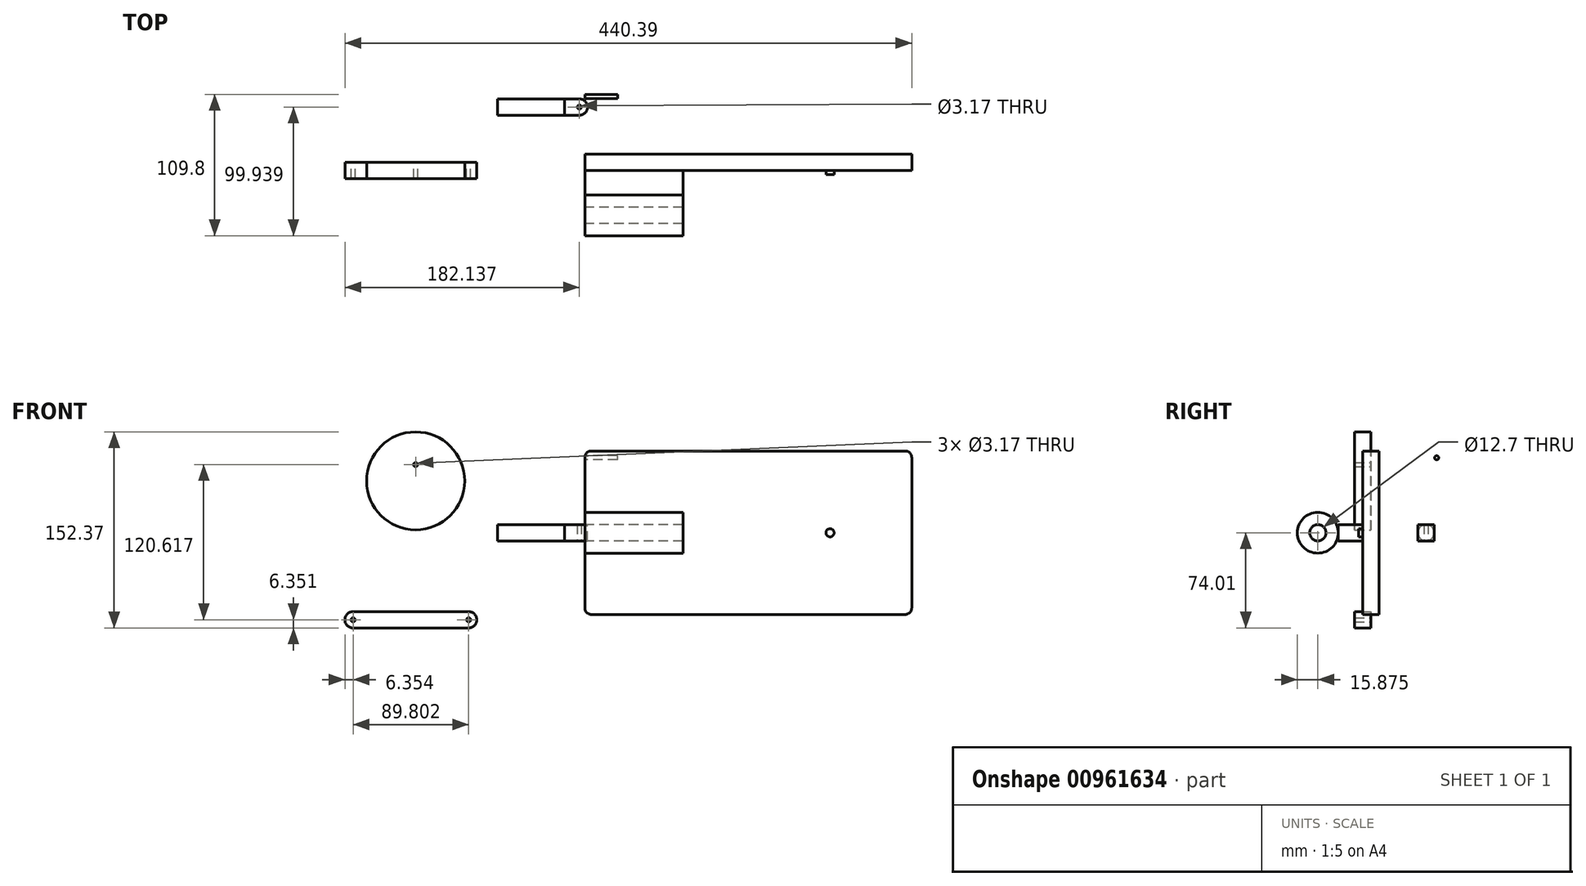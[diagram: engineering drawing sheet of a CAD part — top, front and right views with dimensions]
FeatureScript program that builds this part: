
annotation { "Feature Type Name" : "Feature", "Feature Type Description" : "" }
export const myFeature = defineFeature(function(context is Context, id is Id, definition is map)
    precondition{}
    {
        {
            var Q0;
            Q0=qCreatedBy(makeId("Right.planeOp"),FACE);
            var sketch = newSketch(context, id + "F0", { "sketchPlane" : qUnion([Q0])});
            skLineSegment(sketch, "E0.bottom", {"start": v(6.35, 63.5) * mm, "end": v(-6.35, 63.5) * mm});
            skLineSegment(sketch, "E0.top", {"start": v(6.35, -63.5) * mm, "end": v(-6.35, -63.5) * mm});
            skLineSegment(sketch, "E0.left", {"start": v(6.35, 63.5) * mm, "end": v(6.35, -63.5) * mm});
            skLineSegment(sketch, "E0.right", {"start": v(-6.35, 63.5) * mm, "end": v(-6.35, -63.5) * mm});
            skPoint(sketch, "E0.middle", {"position": v(0, 0) * mm});
            skLineSegment(sketch, "E1", {"start": v(0, 0) * mm, "end": v(-67.64, 0) * mm});
            skLineSegment(sketch, "E2.bottom", {"start": v(-6.35, 0) * mm, "end": v(-25.4, 0) * mm});
            skLineSegment(sketch, "E2.top", {"start": v(-6.35, 6.35) * mm, "end": v(-25.4, 6.35) * mm});
            skLineSegment(sketch, "E2.left", {"start": v(-6.35, 0) * mm, "end": v(-6.35, 6.35) * mm});
            skLineSegment(sketch, "E2.right", {"start": v(-25.4, 0) * mm, "end": v(-25.4, 6.35) * mm});
            skLineSegment(sketch, "E3.MirrorCS", {"start": v(-6.35, -6.35) * mm, "end": v(-25.4, -6.35) * mm});
            skLineSegment(sketch, "E4.MirrorCS", {"start": v(-25.4, 0) * mm, "end": v(-25.4, -6.35) * mm});
            skCircle(sketch, "E5", {"center": v(-41.28, 0) * mm, "radius": 15.88 * mm});
            skCircle(sketch, "E6.0", {"center": v(-41.28, 0) * mm, "radius": 6.35 * mm});
            skLineSegment(sketch, "E7", {"start": v(-6.35, 6.35) * mm, "end": v(-6.35, -6.35) * mm});
            skSolve(sketch);
        }
        {
            var Q0;
            {var subQ1=sQuery(id+"F0.wireOp",EDGE,"E0.bottom");Q0=makeQuery(id+"F0.imprint","IMPRINT",FACE,{"disambiguationData":[TD([[makeQuery(id+"F0.imprint","IMPRINT",EDGE,{"derivedFrom":subQ1}),1.0]])]});}
            extrude(context, id + "F1", {"entities" : qUnion([Q0]), "depth" : 254 * mm, "offsetDistance" : 25.4 * mm});
        }
        {
            var Q0;
            {var subQ3=sQuery(id+"F0.wireOp",EDGE,"E2.top");Q0=makeQuery(id+"F0.imprint","IMPRINT",FACE,{"disambiguationData":[TD([[makeQuery(id+"F0.imprint","IMPRINT",EDGE,{"derivedFrom":subQ3}),1.0]])]});}
            var Q1;
            {var subQ0=sQuery(id+"F0.wireOp",EDGE,"E3.MirrorCS");Q1=makeQuery(id+"F0.imprint","IMPRINT",FACE,{"disambiguationData":[TD([[makeQuery(id+"F0.imprint","IMPRINT",EDGE,{"derivedFrom":subQ0}),-1.0]])]});}
            var Q2;
            {var subQ0=sQuery(id+"F0.wireOp",EDGE,"E5");var subQ1=sQuery(id+"F0.wireOp",EDGE,"E1");var subQ5=makeQuery(id+"F0.imprint","INTERSECT",VERTEX,{"derivedFrom":[subQ1,subQ0]});Q2=makeQuery(id+"F0.imprint","IMPRINT",FACE,{"disambiguationData":[TD([[makeQuery(id+"F0.imprint","IMPRINT",EDGE,{"disambiguationData":[TD([[subQ5,1.0]])],"derivedFrom":subQ1}),1.0]])]});}
            var Q3;
            {var subQ0=sQuery(id+"F0.wireOp",EDGE,"E5");var subQ1=sQuery(id+"F0.wireOp",EDGE,"E1");var subQ5=makeQuery(id+"F0.imprint","INTERSECT",VERTEX,{"derivedFrom":[subQ1,subQ0]});Q3=makeQuery(id+"F0.imprint","IMPRINT",FACE,{"disambiguationData":[TD([[makeQuery(id+"F0.imprint","IMPRINT",EDGE,{"disambiguationData":[TD([[subQ5,1.0]])],"derivedFrom":subQ1}),-1.0]])]});}
            extrude(context, id + "F2", {"entities" : qUnion([Q0, Q1, Q2, Q3]), "operationType" : NewBodyOperationType.ADD, "depth" : 76.2 * mm, "offsetDistance" : 25.4 * mm});
        }
        {
            var Q0;
            Q0=qCreatedBy(makeId("Front.planeOp"),FACE);
            var sketch = newSketch(context, id + "F3", { "sketchPlane" : qUnion([Q0])});
            skCircle(sketch, "E8", {"center": v(-131.44, 40.26) * mm, "radius": 38.1 * mm});
            skCircle(sketch, "E9.0", {"center": v(-131.44, 40.26) * mm, "radius": 3.17 * mm});
            skLineSegment(sketch, "E10", {"start": v(-131.44, 40.26) * mm, "end": v(-131.44, 78.36) * mm});
            skLineSegment(sketch, "E11", {"start": v(-131.44, 40.26) * mm, "end": v(-131.44, 52.96) * mm});
            skCircle(sketch, "E12", {"center": v(-131.44, 52.96) * mm, "radius": 1.59 * mm});
            skSolve(sketch);
        }
        {
            var Q0;
            Q0=qCreatedBy(makeId("Front.planeOp"),FACE);
            cPlane(context, id + "F4", {"entities" : qUnion([Q0]), "cplaneType" : CPlaneType.OFFSET, "offset" : 6.35 * mm, "width" : 152.4 * mm, "height" : 152.4 * mm});
        }
        {
            var Q0;
            Q0=qCreatedBy(id+"F4.planeOp",FACE);
            var sketch = newSketch(context, id + "F5", { "sketchPlane" : qUnion([Q0])});
            skLineSegment(sketch, "E13", {"start": v(0, 0) * mm, "end": v(254, 0) * mm});
            skLineSegment(sketch, "E14", {"start": v(254, 0) * mm, "end": v(190.5, 0) * mm});
            skLineSegment(sketch, "E15", {"start": v(190.5, 0) * mm, "end": v(190.5, 63.5) * mm});
            skLineSegment(sketch, "E16", {"start": v(190.5, 0) * mm, "end": v(190.5, -63.5) * mm});
            skCircle(sketch, "E17", {"center": v(190.5, 0) * mm, "radius": 3.18 * mm});
            skSolve(sketch);
        }
        {
            var Q0;
            Q0=makeQuery(id+"F3.imprint","IMPRINT",FACE,{"disambiguationData":[TD([[makeQuery(id+"F3.imprint","IMPRINT",EDGE,{"derivedFrom":sQuery(id+"F3.wireOp",EDGE,"E8")}),1.0]])]});
            var Q1;
            Q1=makeQuery(id+"F3.imprint","IMPRINT",FACE,{"disambiguationData":[TD([[makeQuery(id+"F3.imprint","IMPRINT",EDGE,{"derivedFrom":sQuery(id+"F3.wireOp",EDGE,"E9.0")}),1.0]])]});
            extrude(context, id + "F6", {"entities" : qUnion([Q0, Q1]), "depth" : 12.7 * mm, "offsetDistance" : 25.4 * mm});
        }
        {
            var Q0;
            Q0=makeQuery(id+"F1.opExtrude","CAP_EDGE",EDGE,{"disambiguationData":[OSD([sQuery(id+"F0.wireOp",EDGE,"E0.bottom")])],"isStart":false});
            var Q1;
            Q1=makeQuery(id+"F1.opExtrude","CAP_EDGE",EDGE,{"disambiguationData":[OSD([sQuery(id+"F0.wireOp",EDGE,"E0.top")])],"isStart":false});
            var Q2;
            Q2=makeQuery(id+"F1.opExtrude","CAP_EDGE",EDGE,{"disambiguationData":[OSD([sQuery(id+"F0.wireOp",EDGE,"E0.top")])],"isStart":true});
            var Q3;
            Q3=makeQuery(id+"F1.opExtrude","CAP_EDGE",EDGE,{"disambiguationData":[OSD([sQuery(id+"F0.wireOp",EDGE,"E0.bottom")])],"isStart":true});
            fillet(context, id + "F7", {"entities" : qUnion([Q0, Q1, Q2, Q3]), "radius" : 5.08 * mm, "tangentPropagation" : true, "allowEdgeOverflow" : false});
        }
        {
            var Q0;
            Q0=qCreatedBy(makeId("Front.planeOp"),FACE);
            var sketch = newSketch(context, id + "F8", { "sketchPlane" : qUnion([Q0])});
            skLineSegment(sketch, "E18.bottom", {"start": v(-186.39, -74) * mm, "end": v(-83.88, -74) * mm});
            skLineSegment(sketch, "E18.top", {"start": v(-186.39, -61.3) * mm, "end": v(-83.88, -61.3) * mm});
            skLineSegment(sketch, "E18.left", {"start": v(-186.39, -74) * mm, "end": v(-186.39, -61.3) * mm});
            skLineSegment(sketch, "E18.right", {"start": v(-83.88, -74) * mm, "end": v(-83.88, -61.3) * mm});
            skLineSegment(sketch, "E19", {"start": v(-83.88, -67.66) * mm, "end": v(-90.23, -67.66) * mm});
            skLineSegment(sketch, "E20", {"start": v(-90.23, -67.66) * mm, "end": v(-90.23, -61.3) * mm});
            skLineSegment(sketch, "E21", {"start": v(-90.23, -67.66) * mm, "end": v(-90.23, -74) * mm});
            skLineSegment(sketch, "E22", {"start": v(-135.13, -61.3) * mm, "end": v(-135.13, -74) * mm});
            skLineSegment(sketch, "E23.MirrorCS", {"start": v(-186.39, -67.66) * mm, "end": v(-180.04, -67.66) * mm});
            skLineSegment(sketch, "E24.MirrorCS", {"start": v(-180.04, -67.66) * mm, "end": v(-180.04, -61.3) * mm});
            skLineSegment(sketch, "E25.MirrorCS", {"start": v(-180.04, -67.66) * mm, "end": v(-180.04, -74) * mm});
            skCircle(sketch, "E26", {"center": v(-90.23, -67.66) * mm, "radius": 1.59 * mm});
            skCircle(sketch, "E27", {"center": v(-180.04, -67.66) * mm, "radius": 1.59 * mm});
            skSolve(sketch);
        }
        {
            var Q0;
            Q0 = qSketchRegion(id + "F8", true);
            extrude(context, id + "F9", {"entities" : qUnion([Q0]), "depth" : 12.7 * mm, "offsetDistance" : 25.4 * mm});
        }
        {
            var Q0;
            Q0=makeQuery(id+"F9.opExtrude","SWEPT_EDGE",EDGE,{"disambiguationData":[OSD([sQuery(id+"F8.wireOp",EDGE,"E18.top"),sQuery(id+"F8.wireOp",EDGE,"E18.right")])]});
            var Q1;
            Q1=makeQuery(id+"F9.opExtrude","SWEPT_EDGE",EDGE,{"disambiguationData":[OSD([sQuery(id+"F8.wireOp",EDGE,"E18.bottom"),sQuery(id+"F8.wireOp",EDGE,"E18.right")])]});
            var Q2;
            Q2=makeQuery(id+"F9.opExtrude","SWEPT_EDGE",EDGE,{"disambiguationData":[OSD([sQuery(id+"F8.wireOp",EDGE,"E18.top"),sQuery(id+"F8.wireOp",EDGE,"E18.left")])]});
            var Q3;
            Q3=makeQuery(id+"F9.opExtrude","SWEPT_EDGE",EDGE,{"disambiguationData":[OSD([sQuery(id+"F8.wireOp",EDGE,"E18.bottom"),sQuery(id+"F8.wireOp",EDGE,"E18.left")])]});
            fillet(context, id + "F10", {"entities" : qUnion([Q0, Q1, Q2, Q3]), "radius" : 6.35 * mm, "tangentPropagation" : true, "allowEdgeOverflow" : false});
        }
        {
            var Q0;
            Q0=qCreatedBy(makeId("Top.planeOp"),FACE);
            var sketch = newSketch(context, id + "F11", { "sketchPlane" : qUnion([Q0])});
            skLineSegment(sketch, "E28.bottom", {"start": v(-67.75, 42.79) * mm, "end": v(2.1, 42.79) * mm});
            skLineSegment(sketch, "E28.top", {"start": v(-67.75, 49.14) * mm, "end": v(2.1, 49.14) * mm});
            skLineSegment(sketch, "E28.left", {"start": v(-67.75, 42.79) * mm, "end": v(-67.75, 49.14) * mm});
            skLineSegment(sketch, "E28.right", {"start": v(2.1, 42.79) * mm, "end": v(2.1, 49.14) * mm});
            skLineSegment(sketch, "E29.bottom", {"start": v(2.1, 42.79) * mm, "end": v(-15.68, 42.79) * mm});
            skLineSegment(sketch, "E29.top", {"start": v(2.1, 36.44) * mm, "end": v(-15.68, 36.44) * mm});
            skLineSegment(sketch, "E29.left", {"start": v(2.1, 42.79) * mm, "end": v(2.1, 36.44) * mm});
            skLineSegment(sketch, "E29.right", {"start": v(-15.68, 42.79) * mm, "end": v(-15.68, 36.44) * mm});
            skLineSegment(sketch, "E30", {"start": v(-15.68, 42.79) * mm, "end": v(-15.68, 49.14) * mm});
            skLineSegment(sketch, "E31", {"start": v(-4.25, 49.14) * mm, "end": v(-4.25, 42.79) * mm});
            skLineSegment(sketch, "E32", {"start": v(-4.25, 42.79) * mm, "end": v(-4.25, 36.44) * mm});
            skCircle(sketch, "E33", {"center": v(-4.25, 42.79) * mm, "radius": 1.59 * mm});
            skSolve(sketch);
        }
        {
            var Q0;
            {var subQ0=sQuery(id+"F11.wireOp",EDGE,"E28.left");Q0=makeQuery(id+"F11.imprint","IMPRINT",FACE,{"disambiguationData":[TD([[makeQuery(id+"F11.imprint","IMPRINT",EDGE,{"derivedFrom":subQ0}),-1.0]])]});}
            var Q1;
            Q1=sQuery(id+"F11.wireOp",EDGE,"E28.bottom");
            revolve(context, id + "F12", {"surfaceOperationType" : NewSurfaceOperationType.NEW, "entities" : qUnion([Q0]), "axis" : qUnion([Q1]), "revolveType" : RevolveType.FULL});
        }
        {
            var Q0;
            {var subQ5=sQuery(id+"F11.wireOp",EDGE,"E30");Q0=makeQuery(id+"F11.imprint","IMPRINT",FACE,{"disambiguationData":[TD([[makeQuery(id+"F11.imprint","IMPRINT",EDGE,{"derivedFrom":subQ5}),-1.0]])]});}
            var Q1;
            {var subQ5=sQuery(id+"F11.wireOp",EDGE,"E28.right");Q1=makeQuery(id+"F11.imprint","IMPRINT",FACE,{"disambiguationData":[TD([[makeQuery(id+"F11.imprint","IMPRINT",EDGE,{"derivedFrom":subQ5}),1.0]])]});}
            var Q2;
            {var subQ3=sQuery(id+"F11.wireOp",EDGE,"E29.left");Q2=makeQuery(id+"F11.imprint","IMPRINT",FACE,{"disambiguationData":[TD([[makeQuery(id+"F11.imprint","IMPRINT",EDGE,{"derivedFrom":subQ3}),-1.0]])]});}
            var Q3;
            {var subQ5=sQuery(id+"F11.wireOp",EDGE,"E29.right");Q3=makeQuery(id+"F11.imprint","IMPRINT",FACE,{"disambiguationData":[TD([[makeQuery(id+"F11.imprint","IMPRINT",EDGE,{"derivedFrom":subQ5}),1.0]])]});}
            extrude(context, id + "F13", {"entities" : qUnion([Q0, Q1, Q2, Q3]), "operationType" : NewBodyOperationType.ADD, "endBound" : BoundingType.SYMMETRIC, "depth" : 12.7 * mm, "offsetDistance" : 25.4 * mm});
        }
        {
            var Q0;
            Q0=makeQuery(id+"F13.opExtrude","SWEPT_EDGE",EDGE,{"disambiguationData":[OSD([sQuery(id+"F11.wireOp",EDGE,"E28.top"),sQuery(id+"F11.wireOp",EDGE,"E28.right")])]});
            var Q1;
            Q1=makeQuery(id+"F13.opExtrude","SWEPT_EDGE",EDGE,{"disambiguationData":[OSD([sQuery(id+"F11.wireOp",EDGE,"E29.top"),sQuery(id+"F11.wireOp",EDGE,"E29.left")])]});
            fillet(context, id + "F14", {"entities" : qUnion([Q0, Q1]), "radius" : 6.35 * mm, "tangentPropagation" : true, "allowEdgeOverflow" : false});
        }
        {
            var Q0;
            {var subQ0=sQuery(id+"F5.wireOp",EDGE,"E15");var subQ3=sQuery(id+"F5.wireOp",EDGE,"E17");var subQ5=makeQuery(id+"F5.imprint","INTERSECT",VERTEX,{"derivedFrom":[subQ0,subQ3]});Q0=makeQuery(id+"F5.imprint","IMPRINT",FACE,{"disambiguationData":[TD([[makeQuery(id+"F5.imprint","IMPRINT",EDGE,{"disambiguationData":[TD([[subQ5,1.0]])],"derivedFrom":subQ3}),1.0]])]});}
            var Q1;
            {var subQ0=sQuery(id+"F5.wireOp",EDGE,"E15");var subQ3=sQuery(id+"F5.wireOp",EDGE,"E17");var subQ5=makeQuery(id+"F5.imprint","INTERSECT",VERTEX,{"derivedFrom":[subQ0,subQ3]});Q1=makeQuery(id+"F5.imprint","IMPRINT",FACE,{"disambiguationData":[TD([[makeQuery(id+"F5.imprint","IMPRINT",EDGE,{"disambiguationData":[TD([[subQ5,-1.0]])],"derivedFrom":subQ3}),1.0]])]});}
            var Q2;
            {var subQ0=sQuery(id+"F5.wireOp",EDGE,"E16");var subQ3=sQuery(id+"F5.wireOp",EDGE,"E17");var subQ5=makeQuery(id+"F5.imprint","INTERSECT",VERTEX,{"derivedFrom":[subQ0,subQ3]});Q2=makeQuery(id+"F5.imprint","IMPRINT",FACE,{"disambiguationData":[TD([[makeQuery(id+"F5.imprint","IMPRINT",EDGE,{"disambiguationData":[TD([[subQ5,1.0]])],"derivedFrom":subQ3}),1.0]])]});}
            var Q3;
            {var subQ0=sQuery(id+"F5.wireOp",EDGE,"E16");var subQ3=sQuery(id+"F5.wireOp",EDGE,"E17");var subQ5=makeQuery(id+"F5.imprint","INTERSECT",VERTEX,{"derivedFrom":[subQ0,subQ3]});Q3=makeQuery(id+"F5.imprint","IMPRINT",FACE,{"disambiguationData":[TD([[makeQuery(id+"F5.imprint","IMPRINT",EDGE,{"disambiguationData":[TD([[subQ5,-1.0]])],"derivedFrom":subQ3}),1.0]])]});}
            extrude(context, id + "F15", {"entities" : qUnion([Q0, Q1, Q2, Q3]), "operationType" : NewBodyOperationType.ADD, "depth" : 3.17 * mm, "offsetDistance" : 25.4 * mm});
        }
        {
            var Q0;
            Q0=qCreatedBy(makeId("Right.planeOp"),FACE);
            var sketch = newSketch(context, id + "F16", { "sketchPlane" : qUnion([Q0])});
            skCircle(sketch, "E34", {"center": v(51.07, 58.25) * mm, "radius": 1.59 * mm});
            skSolve(sketch);
        }
        {
            var Q0;
            Q0 = qSketchRegion(id + "F16", true);
            extrude(context, id + "F17", {"entities" : qUnion([Q0]), "depth" : 25.4 * mm, "offsetDistance" : 25.4 * mm});
        }
    });
